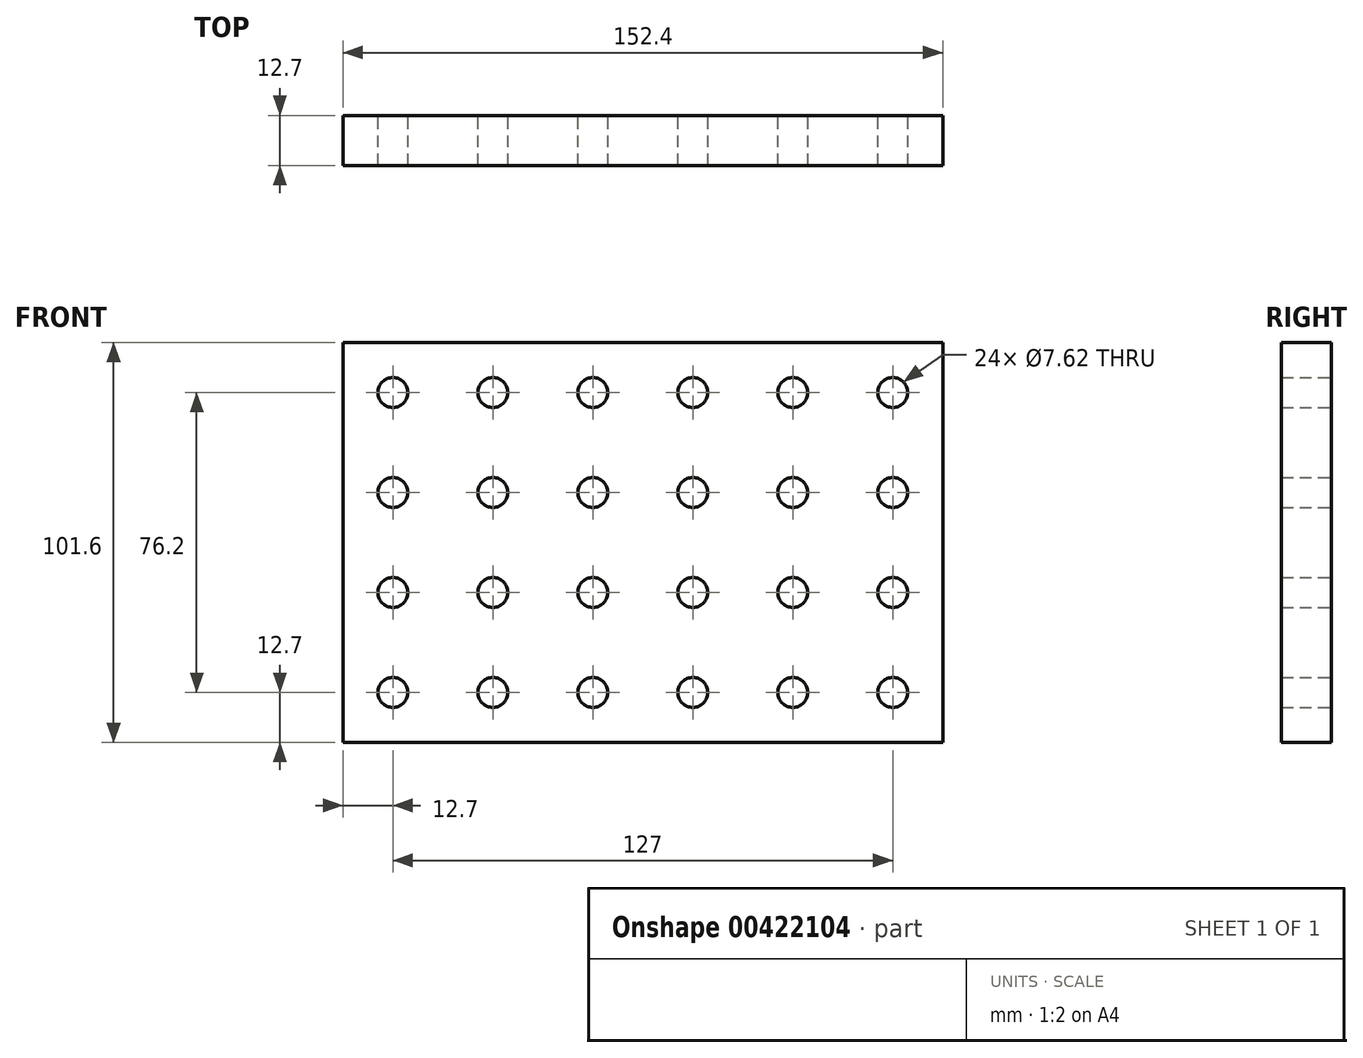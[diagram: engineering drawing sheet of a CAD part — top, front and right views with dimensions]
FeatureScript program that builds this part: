
annotation { "Feature Type Name" : "Feature", "Feature Type Description" : "" }
export const myFeature = defineFeature(function(context is Context, id is Id, definition is map)
    precondition{}
    {
        {
            var Q0;
            Q0=qCreatedBy(makeId("Front.planeOp"),FACE);
            var sketch = newSketch(context, id + "F0", { "sketchPlane" : qUnion([Q0])});
            skLineSegment(sketch, "E0.bottom", {"start": v(0, 0) * mm, "end": v(152.4, 0) * mm});
            skLineSegment(sketch, "E0.top", {"start": v(0, 101.6) * mm, "end": v(152.4, 101.6) * mm});
            skLineSegment(sketch, "E0.left", {"start": v(0, 0) * mm, "end": v(0, 101.6) * mm});
            skLineSegment(sketch, "E0.right", {"start": v(152.4, 0) * mm, "end": v(152.4, 101.6) * mm});
            skSolve(sketch);
        }
        {
            var Q0;
            Q0=makeQuery(id+"F0.imprint","IMPRINT",FACE,{"disambiguationData":[TD([[makeQuery(id+"F0.imprint","IMPRINT",EDGE,{"derivedFrom":sQuery(id+"F0.wireOp",EDGE,"E0.bottom")}),1.0]])]});
            var sketch = newSketch(context, id + "F1", { "sketchPlane" : qUnion([Q0])});
            skLineSegment(sketch, "E1.bottom", {"start": v(0, 0) * mm, "end": v(12.7, 0) * mm, "construction": true});
            skLineSegment(sketch, "E1.top", {"start": v(0, 12.7) * mm, "end": v(12.7, 12.7) * mm, "construction": true});
            skLineSegment(sketch, "E1.left", {"start": v(0, 0) * mm, "end": v(0, 12.7) * mm, "construction": true});
            skLineSegment(sketch, "E1.right", {"start": v(12.7, 0) * mm, "end": v(12.7, 12.7) * mm, "construction": true});
            skCircle(sketch, "E2", {"center": v(12.7, 12.7) * mm, "radius": 3.81 * mm});
            skCircle(sketch, "E3.0.1.0", {"center": v(12.7, 38.1) * mm, "radius": 3.81 * mm});
            skCircle(sketch, "E3.0.2.0", {"center": v(12.7, 63.5) * mm, "radius": 3.81 * mm});
            skCircle(sketch, "E3.0.3.0", {"center": v(12.7, 88.9) * mm, "radius": 3.81 * mm});
            skCircle(sketch, "E3.1.0.0", {"center": v(38.1, 12.7) * mm, "radius": 3.81 * mm});
            skCircle(sketch, "E3.1.1.0", {"center": v(38.1, 38.1) * mm, "radius": 3.81 * mm});
            skCircle(sketch, "E3.1.2.0", {"center": v(38.1, 63.5) * mm, "radius": 3.81 * mm});
            skCircle(sketch, "E3.1.3.0", {"center": v(38.1, 88.9) * mm, "radius": 3.81 * mm});
            skCircle(sketch, "E3.2.0.0", {"center": v(63.5, 12.7) * mm, "radius": 3.81 * mm});
            skCircle(sketch, "E3.2.1.0", {"center": v(63.5, 38.1) * mm, "radius": 3.81 * mm});
            skCircle(sketch, "E3.2.2.0", {"center": v(63.5, 63.5) * mm, "radius": 3.81 * mm});
            skCircle(sketch, "E3.2.3.0", {"center": v(63.5, 88.9) * mm, "radius": 3.81 * mm});
            skCircle(sketch, "E3.3.0.0", {"center": v(88.9, 12.7) * mm, "radius": 3.81 * mm});
            skCircle(sketch, "E3.3.1.0", {"center": v(88.9, 38.1) * mm, "radius": 3.81 * mm});
            skCircle(sketch, "E3.3.2.0", {"center": v(88.9, 63.5) * mm, "radius": 3.81 * mm});
            skCircle(sketch, "E3.3.3.0", {"center": v(88.9, 88.9) * mm, "radius": 3.81 * mm});
            skCircle(sketch, "E3.4.0.0", {"center": v(114.3, 12.7) * mm, "radius": 3.81 * mm});
            skCircle(sketch, "E3.4.1.0", {"center": v(114.3, 38.1) * mm, "radius": 3.81 * mm});
            skCircle(sketch, "E3.4.2.0", {"center": v(114.3, 63.5) * mm, "radius": 3.81 * mm});
            skCircle(sketch, "E3.4.3.0", {"center": v(114.3, 88.9) * mm, "radius": 3.81 * mm});
            skCircle(sketch, "E3.5.0.0", {"center": v(139.7, 12.7) * mm, "radius": 3.81 * mm});
            skCircle(sketch, "E3.5.1.0", {"center": v(139.7, 38.1) * mm, "radius": 3.81 * mm});
            skCircle(sketch, "E3.5.2.0", {"center": v(139.7, 63.5) * mm, "radius": 3.81 * mm});
            skCircle(sketch, "E3.5.3.0", {"center": v(139.7, 88.9) * mm, "radius": 3.81 * mm});
            skLineSegment(sketch, "E3.direction1", {"start": v(12.7, 12.7) * mm, "end": v(38.1, 12.7) * mm, "construction": true});
            skLineSegment(sketch, "E3.direction2", {"start": v(12.7, 12.7) * mm, "end": v(12.7, 38.1) * mm, "construction": true});
            skSolve(sketch);
        }
        {
            var Q0;
            Q0 = qSketchRegion(id + "F0", true);
            extrude(context, id + "F2", {"entities" : qUnion([Q0]), "depth" : 12.7 * mm});
        }
        {
            var Q0;
            Q0 = qSketchRegion(id + "F1", true);
            extrude(context, id + "F3", {"entities" : qUnion([Q0]), "operationType" : NewBodyOperationType.REMOVE, "depth" : 25.4 * mm});
        }
    });
